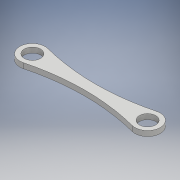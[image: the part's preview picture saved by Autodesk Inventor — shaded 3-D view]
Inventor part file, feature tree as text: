
AUTODESK INVENTOR PART (.ipt)
format: ipt  version: 2017 (Build 210142000, 142)  size: 229,888 bytes
history: native  units: mm
features: extrude x1, sketch x1
ambient origin geometry x8: Origin, YZ Plane, XZ Plane, XY Plane, X Axis, Y Axis, Z Axis, Center Point
bodies: Solid1 (feature_tree)
feature tree (2):
  extrude  "Extrusion1"  Depth=7.0mm
  sketch  "Sketch1"  dims[d0=22.0mm d1=22.0mm d2=155.0mm d3=77.5mm d4=6.0mm d5=6.0mm d6=7.0mm d7=0.0mm]
